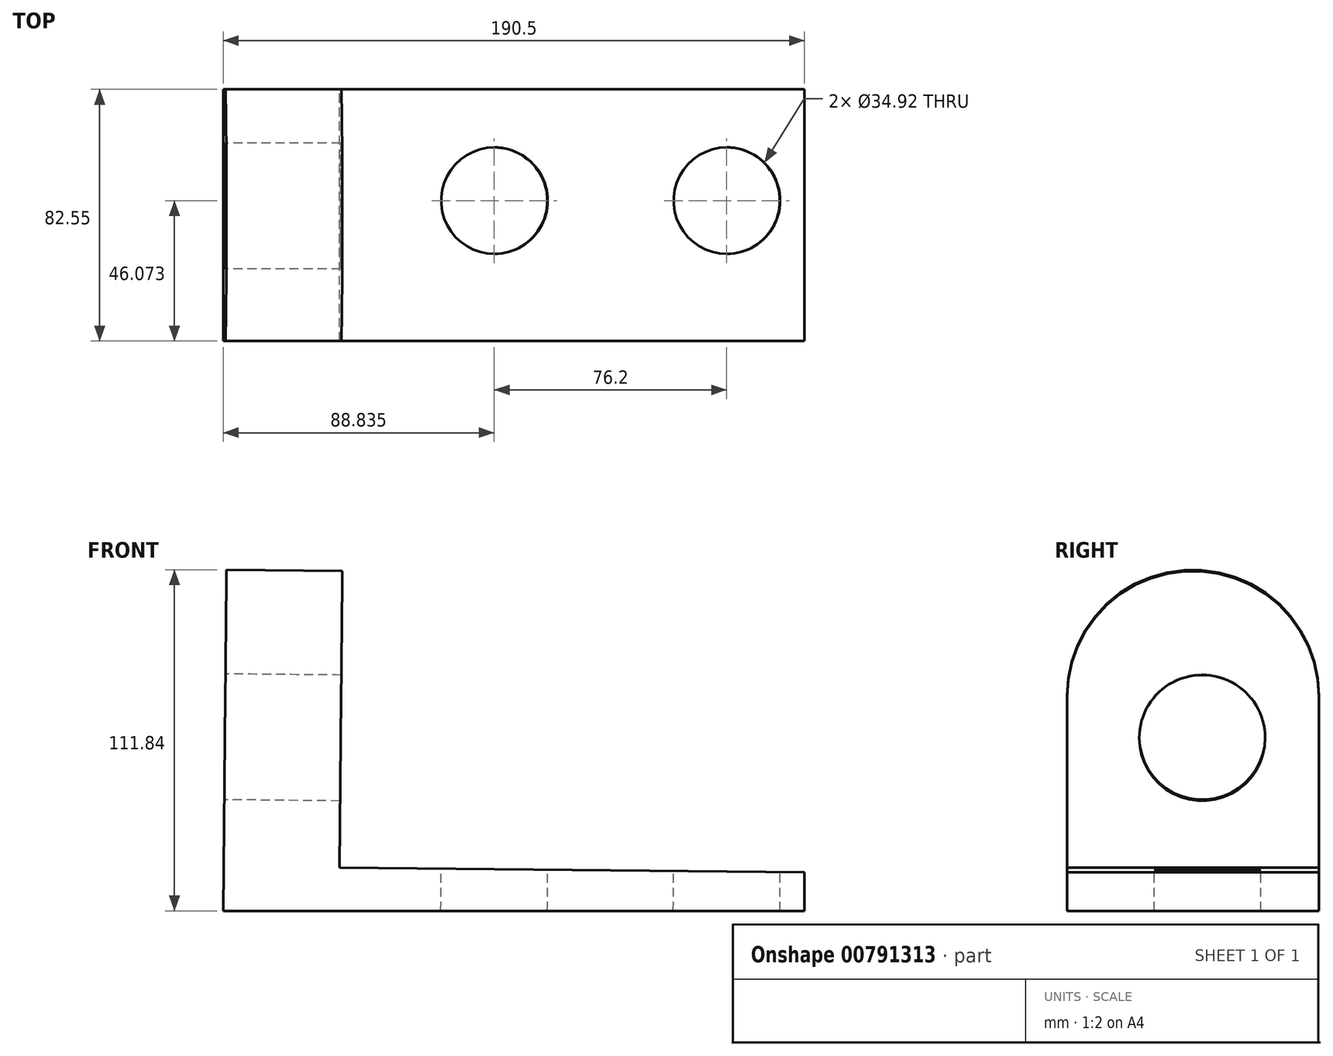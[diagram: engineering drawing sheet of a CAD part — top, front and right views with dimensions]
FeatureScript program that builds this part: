
annotation { "Feature Type Name" : "Feature", "Feature Type Description" : "" }
export const myFeature = defineFeature(function(context is Context, id is Id, definition is map)
    precondition{}
    {
        {
            var Q0;
            Q0=qCreatedBy(makeId("Front.planeOp"),FACE);
            var sketch = newSketch(context, id + "F0", { "sketchPlane" : qUnion([Q0])});
            skLineSegment(sketch, "E0", {"start": v(-75.98, 0) * mm, "end": v(114.52, 0) * mm});
            skLineSegment(sketch, "E1", {"start": v(114.52, 0) * mm, "end": v(114.52, 12.7) * mm});
            skLineSegment(sketch, "E2", {"start": v(114.52, 12.7) * mm, "end": v(-37.88, 14.14) * mm});
            skLineSegment(sketch, "E3", {"start": v(-37.88, 14.14) * mm, "end": v(-36.68, 141.13) * mm});
            skLineSegment(sketch, "E4", {"start": v(-75.98, 0) * mm, "end": v(-74.65, 141.13) * mm});
            skLineSegment(sketch, "E5", {"start": v(-74.65, 141.13) * mm, "end": v(-36.68, 141.13) * mm});
            skSolve(sketch);
        }
        {
            var Q0;
            Q0 = qSketchRegion(id + "F0", true);
            extrude(context, id + "F1", {"entities" : qUnion([Q0]), "depth" : 82.55 * mm, "offsetDistance" : 25.4 * mm});
        }
        {
            var Q0;
            Q0=makeQuery(id+"F1.opExtrude","SWEPT_FACE",FACE,{"disambiguationData":[OSD([sQuery(id+"F0.wireOp",EDGE,"E2")])]});
            var sketch = newSketch(context, id + "F2", { "sketchPlane" : qUnion([Q0])});
            skLineSegment(sketch, "E6", {"start": v(-38, -36.48) * mm, "end": v(12.8, -36.48) * mm, "construction": true});
            skLineSegment(sketch, "E7", {"start": v(12.8, -36.48) * mm, "end": v(89, -36.48) * mm, "construction": true});
            skCircle(sketch, "E8", {"center": v(12.8, -36.48) * mm, "radius": 17.46 * mm});
            skCircle(sketch, "E9", {"center": v(89, -36.48) * mm, "radius": 17.46 * mm});
            skSolve(sketch);
        }
        {
            var Q0;
            Q0 = qSketchRegion(id + "F2", true);
            extrude(context, id + "F3", {"entities" : qUnion([Q0]), "operationType" : NewBodyOperationType.REMOVE, "oppositeDirection" : true, "depth" : 25.4 * mm, "offsetDistance" : 25.4 * mm});
        }
        {
            var Q0;
            Q0=makeQuery(id+"F1.opExtrude","SWEPT_FACE",FACE,{"disambiguationData":[OSD([sQuery(id+"F0.wireOp",EDGE,"E4")])]});
            var sketch = newSketch(context, id + "F4", { "sketchPlane" : qUnion([Q0])});
            skLineSegment(sketch, "E10", {"start": v(82.55, -0.72) * mm, "end": v(82.55, 69.85) * mm, "construction": true});
            skArc(sketch, "E11", {"start": v(82.55, 69.85) * mm, "mid": v(41.28, 111.13) * mm, "end": v(0, 69.85) * mm});
            skSolve(sketch);
        }
        {
            var Q0;
            Q0 = qSketchRegion(id + "F4", true);
            var Q1;
            Q1=makeQuery(id+"F1.opExtrude","SWEPT_FACE",FACE,{"disambiguationData":[OSD([sQuery(id+"F0.wireOp",EDGE,"E5")])]});
            extrude(context, id + "F5", {"entities" : qUnion([Q0, Q1]), "operationType" : NewBodyOperationType.REMOVE, "oppositeDirection" : true, "depth" : 25.4 * mm, "offsetDistance" : 25.4 * mm});
        }
        {
            var Q0;
            {var subQ0=sQuery(id+"F4.wireOp",EDGE,"E11");Q0=makeQuery(id+"F4.imprint","IMPRINT",FACE,{"disambiguationData":[TD([[makeQuery(id+"F4.imprint","IMPRINT",EDGE,{"derivedFrom":subQ0}),-1.0]])]});}
            extrude(context, id + "F6", {"entities" : qUnion([Q0]), "operationType" : NewBodyOperationType.REMOVE, "endBound" : BoundingType.UP_TO_NEXT, "oppositeDirection" : true, "depth" : 25.4 * mm, "offsetDistance" : 25.4 * mm});
        }
        {
            var Q0;
            Q0=makeQuery(id+"F1.opExtrude","SWEPT_FACE",FACE,{"disambiguationData":[OSD([sQuery(id+"F0.wireOp",EDGE,"E4")])]});
            var sketch = newSketch(context, id + "F7", { "sketchPlane" : qUnion([Q0])});
            skLineSegment(sketch, "E12", {"start": v(41.28, -0.72) * mm, "end": v(38.22, 56.35) * mm, "construction": true});
            skCircle(sketch, "E13", {"center": v(38.22, 56.35) * mm, "radius": 20.64 * mm});
            skSolve(sketch);
        }
        {
            var Q0;
            Q0=makeQuery(id+"F7.imprint","IMPRINT",FACE,{"disambiguationData":[TD([[makeQuery(id+"F7.imprint","IMPRINT",EDGE,{"derivedFrom":sQuery(id+"F7.wireOp",EDGE,"E13")}),1.0]])]});
            extrude(context, id + "F8", {"entities" : qUnion([Q0]), "operationType" : NewBodyOperationType.REMOVE, "endBound" : BoundingType.UP_TO_NEXT, "oppositeDirection" : true, "depth" : 25.4 * mm, "offsetDistance" : 25.4 * mm});
        }
    });
